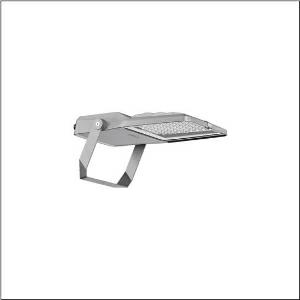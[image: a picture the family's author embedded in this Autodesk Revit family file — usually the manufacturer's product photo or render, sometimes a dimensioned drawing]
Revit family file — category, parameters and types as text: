
# Revit family: floodlight_fl_21_iq_mini___pl64_5xa7772c2e1a_df54
name_source: partatom
category: Lighting Fixtures
units: mm (PartAtom-declared; Revit-internal decimal feet)

## family parameters
Cut with Voids When Loaded = No
Host = Face
Light Source = No
Part Type = Normal
Room Calculation Point = No
Round Connector Dimension = Use Diameter
Shared = No

## types (1)
- --- (1 x LED, 11790 lm, 87.2 W, 3000K)
    Apparent Load = 87 VA
    CIE Flux Codes = 28 80 98 100 100
    Color Rendering = 70
    Color Temperature = 3000K
    Default Elevation = 1800 mm
    Description = Floodlight FL 21 iQ mini, floodlight, primary light control with lens, of PMMA, primary optical cover: protective disc, of toughened safety glass, transparent, light distribution: PL64, light emission: direct distribution, installation type: surface-mounted, LED, High Power LED, rated luminous flux: 11.790lm, luminous efficacy: 135lm/W, light colour: 730, colour temperature: 3000K, control gear: iQ Street-Remote/DALI, control: Street-Remote, Auto-Match, Temp-Guard, Night-Set, Smart-Wire, Desk-Remote (wireless, voltage-free reading and setting of iQ features in the workshop via application-optimized NFC function/RFID function), optimised constant luminous flux control (CLO 2.0), with terminal, 6-pole, mains connection: 220..240V, AC, 50/60Hz, start of lifetime: 87W, end of service life: 92W, reduction: 40W, luminaire housing, of diecast aluminium, powder-coated, Siteco® metallic grey (DB 702S), corrosivity category C5 mid according to DIN EN ISO 12944, suitable for swimming pools, chlorine-resistant, sealing non-destructively replaceable, mounting bracket, of steel, galvanised, powder-coated, Siteco® metallic grey (DB 702S), protection rating (complete): IP66, insulation class (complete): insulation class II (safety insulation), certification: CE, ENEC, VDE, protection symbol: D, impact resistance: IK08, permissible operating ambient temperature: -40..+40°C, permissible operating ambient temperature for outdoor applications: -40..+50°C, standard: DIN EN 12944, LABS conformity tested according to VDMA 24364:2018-05, packaging unit: 1 piece

Light Distribution: PL64
    Height = 70 mm
    Lamp = 1 x LED
    Lamp Light Flux = 11790 lm
    Lamp Power = 87.2 W
    Lamp count = 1
    Length = 485 mm
    Luminous efficacy = 135 lm/W
    Manufacturer = Siteco
    ModVariant = No
    Model = 5XA7772C2E1A
    Number of Poles = 1
    OnlyDefault = Yes
    Power Factor = 1
    Product Name = Floodlight FL 21 iQ mini | PL64
    Product group = floodlight | pylon annexe
    ProductGroupID = 6200
    Protection Class = Protection class II
    Protection Degree = IP 66
    RLX_Detail_Level = 1
    RLX_Emergency_Light_Flux = 0 lm
    RLX_Emergency_Type = 0
    RLX_Emergency_Type_DB = No
    RlxData = <blob elided: 96341 chars, md5=83d4325b>
    Socket = socket
    Standby Power = 0 W
    System Light Flux = 11790 lm
    System Power = 87 W
    Type Comments = factory setting: luminous flux: 100 % | dim-lin: 254 | 456 mA
    Type Image = l_1006845.jpg
    URL = http://relux.com
    VarID = @adj_166434
    Voltage = 0 V
    Weight = 0.00 kg
    Width = 337 mm

## geometry (parser evidence)
native form markers: Blend x4, Sweep x12
no freeform markers — native parametric forms only
